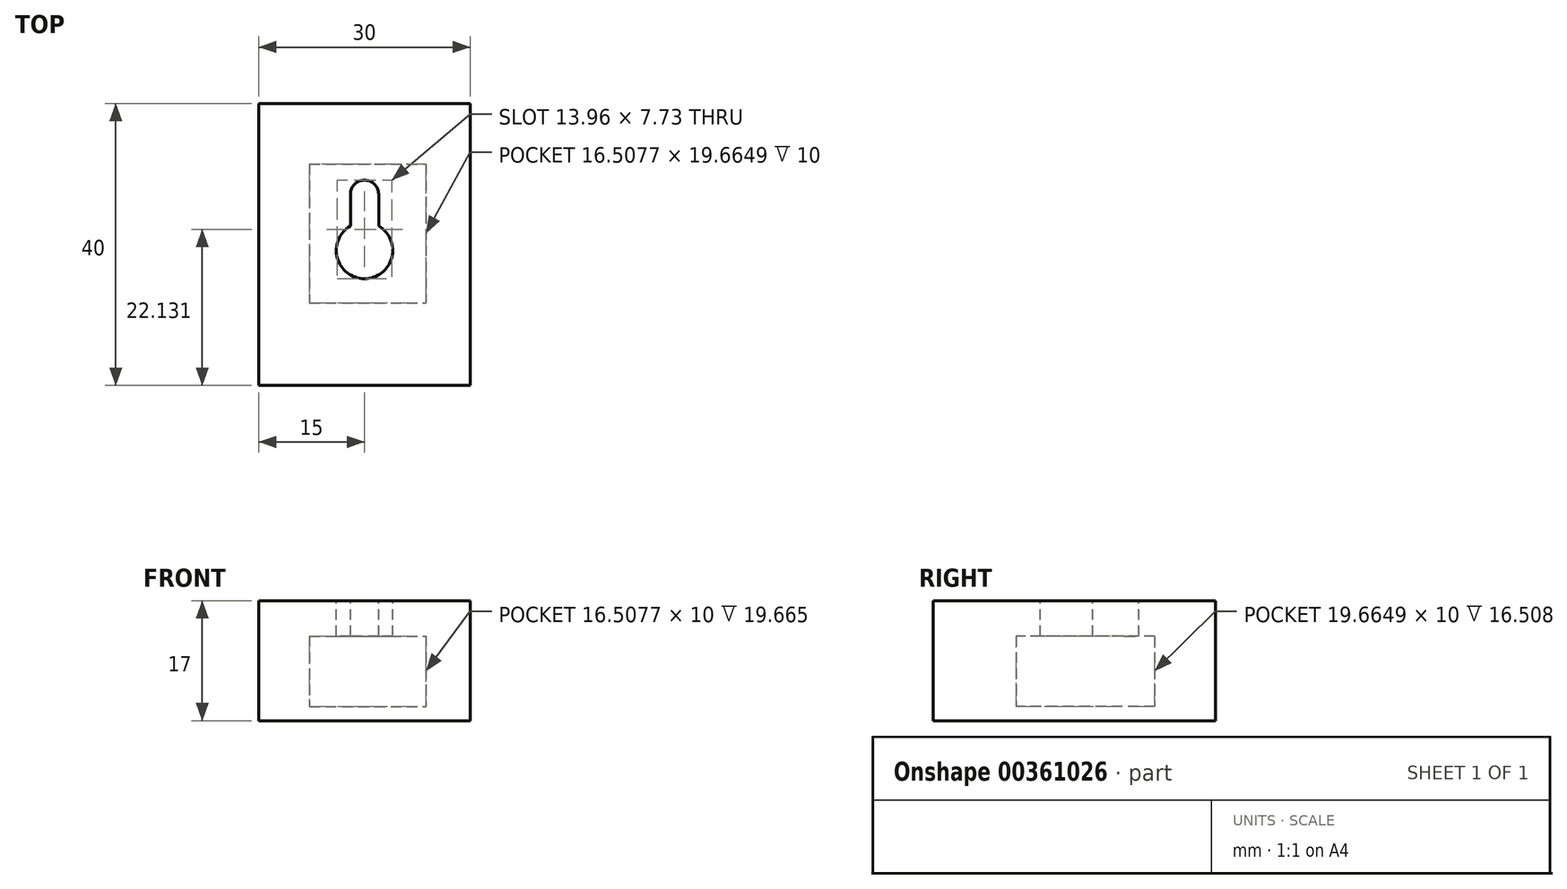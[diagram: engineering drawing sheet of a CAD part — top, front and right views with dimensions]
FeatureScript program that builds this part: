
annotation { "Feature Type Name" : "Feature", "Feature Type Description" : "" }
export const myFeature = defineFeature(function(context is Context, id is Id, definition is map)
    precondition{}
    {
        {
            var Q0;
            Q0=qCreatedBy(makeId("Top.planeOp"),FACE);
            var sketch = newSketch(context, id + "F0", { "sketchPlane" : qUnion([Q0])});
            skLineSegment(sketch, "E0.bottom", {"start": v(0, 0) * mm, "end": v(30, 0) * mm});
            skLineSegment(sketch, "E0.top", {"start": v(0, 40) * mm, "end": v(30, 40) * mm});
            skLineSegment(sketch, "E0.left", {"start": v(0, 0) * mm, "end": v(0, 40) * mm});
            skLineSegment(sketch, "E0.right", {"start": v(30, 0) * mm, "end": v(30, 40) * mm});
            skSolve(sketch);
        }
        {
            var Q0;
            Q0=makeQuery(id+"F0.imprint","IMPRINT",FACE,{"disambiguationData":[TD([[makeQuery(id+"F0.imprint","IMPRINT",EDGE,{"derivedFrom":sQuery(id+"F0.wireOp",EDGE,"E0.bottom")}),1.0]])]});
            extrude(context, id + "F1", {"entities" : qUnion([Q0]), "depth" : 17 * mm});
        }
        {
            var Q0;
            Q0=makeQuery(id+"F1.opExtrude","CAP_FACE",FACE,{"disambiguationData":[OSD([sQuery(id+"F0.wireOp",EDGE,"E0.bottom"),sQuery(id+"F0.wireOp",EDGE,"E0.top"),sQuery(id+"F0.wireOp",EDGE,"E0.left"),sQuery(id+"F0.wireOp",EDGE,"E0.right")])],"isStart":false});
            var sketch = newSketch(context, id + "F2", { "sketchPlane" : qUnion([Q0])});
            skArc(sketch, "E1", {"start": v(13, 22.61) * mm, "mid": v(15, 15.15) * mm, "end": v(17, 22.61) * mm});
            skLineSegment(sketch, "E2", {"start": v(13, 22.61) * mm, "end": v(13, 27.11) * mm});
            skLineSegment(sketch, "E3", {"start": v(17, 22.61) * mm, "end": v(17, 27.11) * mm});
            skArc(sketch, "E4", {"start": v(17, 27.11) * mm, "mid": v(15, 29.11) * mm, "end": v(13, 27.11) * mm});
            skSolve(sketch);
        }
        {
            var Q0;
            Q0=makeQuery(id+"F2.imprint","IMPRINT",FACE,{"disambiguationData":[TD([[makeQuery(id+"F2.imprint","IMPRINT",EDGE,{"derivedFrom":sQuery(id+"F2.wireOp",EDGE,"E1")}),1.0]])]});
            extrude(context, id + "F3", {"entities" : qUnion([Q0]), "operationType" : NewBodyOperationType.REMOVE, "oppositeDirection" : true, "depth" : 15 * mm});
        }
        {
            var Q0;
            Q0=makeQuery(id+"F3.boolean.opBoolean","COPY",FACE,{"derivedFrom":makeQuery(id+"F3.opExtrude","CAP_FACE",FACE,{"disambiguationData":[OSD([sQuery(id+"F2.wireOp",EDGE,"E1"),sQuery(id+"F2.wireOp",EDGE,"E2"),sQuery(id+"F2.wireOp",EDGE,"E3"),sQuery(id+"F2.wireOp",EDGE,"E4")])],"isStart":false})});
            var sketch = newSketch(context, id + "F4", { "sketchPlane" : qUnion([Q0])});
            skLineSegment(sketch, "E5.bottom", {"start": v(7.22, 31.37) * mm, "end": v(23.73, 31.37) * mm});
            skLineSegment(sketch, "E5.top", {"start": v(7.22, 11.7) * mm, "end": v(23.73, 11.7) * mm});
            skLineSegment(sketch, "E5.left", {"start": v(7.22, 31.37) * mm, "end": v(7.22, 11.7) * mm});
            skLineSegment(sketch, "E5.right", {"start": v(23.73, 31.37) * mm, "end": v(23.73, 11.7) * mm});
            skSolve(sketch);
        }
        {
            var Q0;
            Q0 = qSketchRegion(id + "F4", true);
            extrude(context, id + "F5", {"entities" : qUnion([Q0]), "operationType" : NewBodyOperationType.REMOVE, "depth" : 10 * mm});
        }
    });
